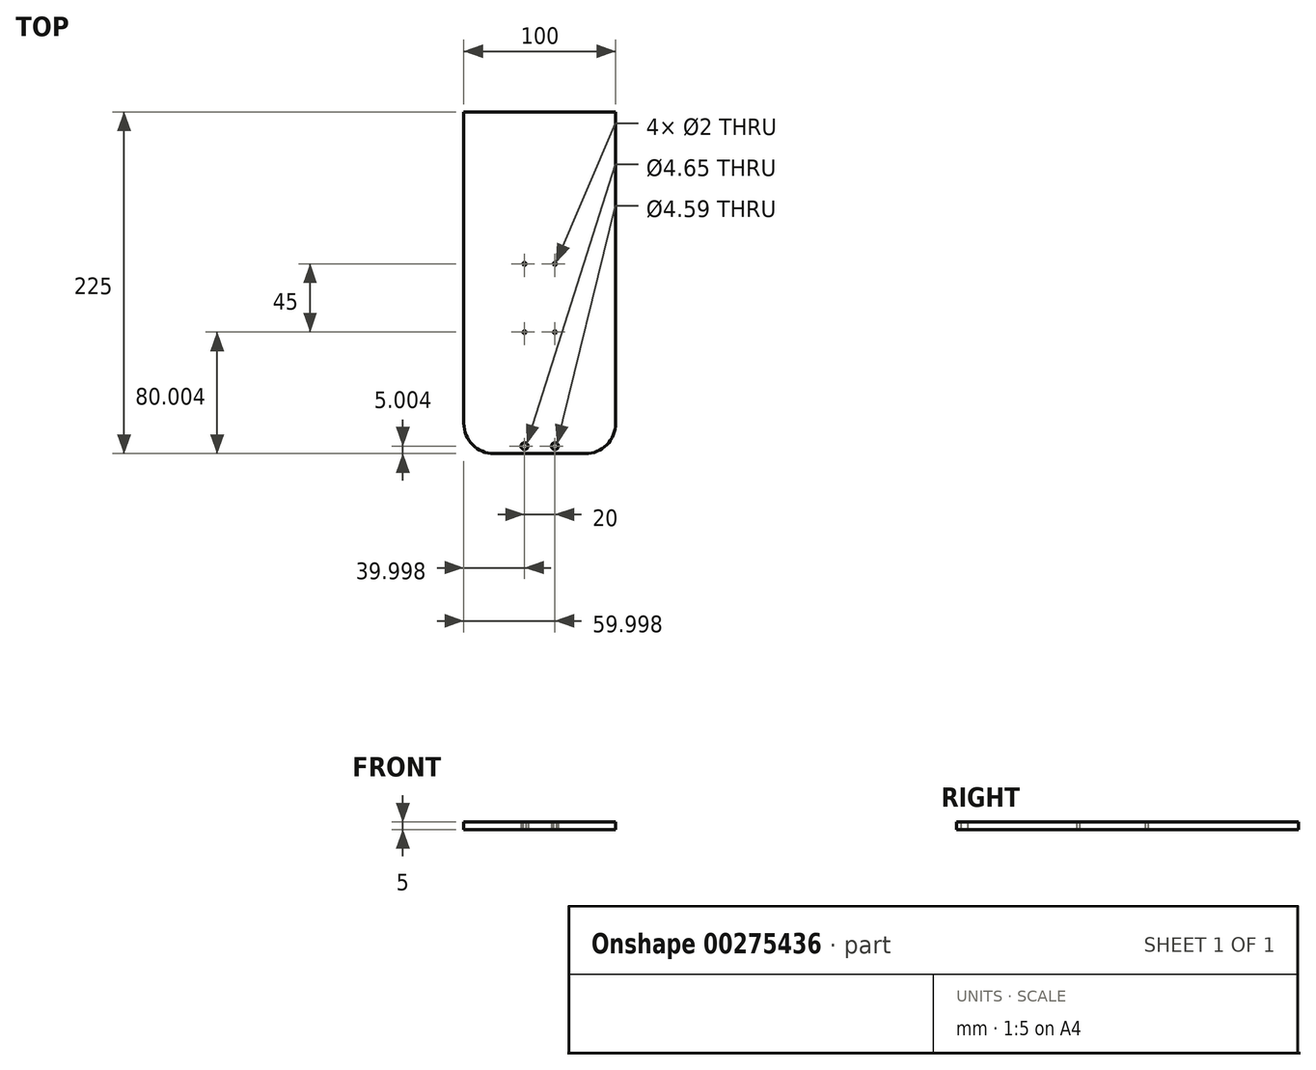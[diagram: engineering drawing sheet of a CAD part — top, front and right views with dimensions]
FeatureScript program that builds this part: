
annotation { "Feature Type Name" : "Feature", "Feature Type Description" : "" }
export const myFeature = defineFeature(function(context is Context, id is Id, definition is map)
    precondition{}
    {
        {
            var Q0;
            Q0=qCreatedBy(makeId("Top.planeOp"),FACE);
            var sketch = newSketch(context, id + "F0", { "sketchPlane" : qUnion([Q0])});
            skLineSegment(sketch, "E0.bottom", {"start": v(-38.9, 102.67) * mm, "end": v(61.1, 102.67) * mm});
            skLineSegment(sketch, "E0.top", {"start": v(-18.9, -122.33) * mm, "end": v(41.1, -122.33) * mm});
            skLineSegment(sketch, "E0.left", {"start": v(-38.9, 102.67) * mm, "end": v(-38.9, -102.33) * mm});
            skLineSegment(sketch, "E0.right", {"start": v(61.1, 102.67) * mm, "end": v(61.1, -102.33) * mm});
            skLineSegment(sketch, "E1", {"start": v(-38.9, -82.33) * mm, "end": v(61.1, -82.33) * mm});
            skLineSegment(sketch, "E2", {"start": v(-28.9, -77.33) * mm, "end": v(-18.9, -77.33) * mm});
            skLineSegment(sketch, "E3", {"start": v(-28.9, -32.33) * mm, "end": v(-18.9, -32.33) * mm});
            skLineSegment(sketch, "E4", {"start": v(-38.9, 12.67) * mm, "end": v(61.1, 12.67) * mm});
            skLineSegment(sketch, "E5", {"start": v(11.1, -122.33) * mm, "end": v(11.1, 114.69) * mm, "construction": true});
            skPoint(sketch, "E5.endSnap0", {"position": v(11.1, 102.67) * mm});
            skLineSegment(sketch, "E6.top", {"start": v(26.1, 7.67) * mm, "end": v(-3.9, 7.67) * mm});
            skLineSegment(sketch, "E6.left", {"start": v(31.1, -32.33) * mm, "end": v(31.1, 2.67) * mm});
            skLineSegment(sketch, "E6.right", {"start": v(-8.9, -32.33) * mm, "end": v(-8.9, 2.67) * mm});
            skLineSegment(sketch, "E7.top", {"start": v(-3.9, -37.33) * mm, "end": v(26.1, -37.33) * mm});
            skLineSegment(sketch, "E7.left", {"start": v(-8.9, -77.33) * mm, "end": v(-8.9, -42.33) * mm});
            skLineSegment(sketch, "E7.right", {"start": v(31.1, -77.33) * mm, "end": v(31.1, -42.33) * mm});
            skPoint(sketch, "E8.visualSharp", {"position": v(-8.9, 7.67) * mm});
            skArc(sketch, "E8.filletArc", {"start": v(-3.9, 7.67) * mm, "mid": v(-7.44, 6.2) * mm, "end": v(-8.9, 2.67) * mm});
            skPoint(sketch, "E9.visualSharp", {"position": v(31.1, 7.67) * mm});
            skArc(sketch, "E9.filletArc", {"start": v(31.1, 2.67) * mm, "mid": v(29.63, 6.2) * mm, "end": v(26.1, 7.67) * mm});
            skPoint(sketch, "E10.visualSharp", {"position": v(-8.9, -37.33) * mm});
            skArc(sketch, "E10.filletArc", {"start": v(-3.9, -37.33) * mm, "mid": v(-7.44, -38.8) * mm, "end": v(-8.9, -42.33) * mm});
            skPoint(sketch, "E11.visualSharp", {"position": v(31.1, -37.33) * mm});
            skArc(sketch, "E11.filletArc", {"start": v(31.1, -42.33) * mm, "mid": v(29.63, -38.8) * mm, "end": v(26.1, -37.33) * mm});
            skCircle(sketch, "E12", {"center": v(1.1, 2.67) * mm, "radius": 1 * mm});
            skCircle(sketch, "E13", {"center": v(21.1, 2.67) * mm, "radius": 1 * mm});
            skCircle(sketch, "E14", {"center": v(1.1, -42.33) * mm, "radius": 1 * mm});
            skCircle(sketch, "E15", {"center": v(21.1, -42.33) * mm, "radius": 1 * mm});
            skPoint(sketch, "E16.visualSharp", {"position": v(-38.9, -122.33) * mm});
            skArc(sketch, "E16.filletArc", {"start": v(-38.9, -102.33) * mm, "mid": v(-33.04, -116.47) * mm, "end": v(-18.9, -122.33) * mm});
            skPoint(sketch, "E17.visualSharp", {"position": v(61.1, -122.33) * mm});
            skArc(sketch, "E17.filletArc", {"start": v(41.1, -122.33) * mm, "mid": v(55.24, -116.47) * mm, "end": v(61.1, -102.33) * mm});
            skCircle(sketch, "E18", {"center": v(1.1, -117.33) * mm, "radius": 2.33 * mm});
            skCircle(sketch, "E19", {"center": v(21.1, -117.33) * mm, "radius": 2.3 * mm});
            skLineSegment(sketch, "E20.bottom", {"start": v(-26.9, -32.33) * mm, "end": v(-20.9, -32.33) * mm});
            skLineSegment(sketch, "E20.left", {"start": v(-28.9, -30.33) * mm, "end": v(-28.9, 7.67) * mm});
            skLineSegment(sketch, "E20.right", {"start": v(-18.9, -30.33) * mm, "end": v(-18.9, 7.67) * mm});
            skLineSegment(sketch, "E21.trimOffspring", {"start": v(43.1, -32.33) * mm, "end": v(49.1, -32.33) * mm});
            skPoint(sketch, "E22.visualSharp", {"position": v(-28.9, -32.33) * mm});
            skArc(sketch, "E22.filletArc", {"start": v(-28.9, -30.33) * mm, "mid": v(-28.32, -31.74) * mm, "end": v(-26.9, -32.33) * mm});
            skPoint(sketch, "E23.visualSharp", {"position": v(-18.9, -32.33) * mm});
            skArc(sketch, "E23.filletArc", {"start": v(-20.9, -32.33) * mm, "mid": v(-19.49, -31.74) * mm, "end": v(-18.9, -30.33) * mm});
            skLineSegment(sketch, "E24.MirrorCS", {"start": v(51.1, -30.33) * mm, "end": v(51.1, 7.67) * mm});
            skLineSegment(sketch, "E25.MirrorCS", {"start": v(41.1, -30.33) * mm, "end": v(41.1, 7.67) * mm});
            skLineSegment(sketch, "E26.MirrorCS", {"start": v(49.1, -32.33) * mm, "end": v(43.1, -32.33) * mm});
            skArc(sketch, "E27.MirrorCS", {"start": v(43.1, -32.33) * mm, "mid": v(41.68, -31.74) * mm, "end": v(41.1, -30.33) * mm});
            skArc(sketch, "E28.MirrorCS", {"start": v(51.1, -30.33) * mm, "mid": v(50.51, -31.74) * mm, "end": v(49.1, -32.33) * mm});
            skLineSegment(sketch, "E29.top", {"start": v(-26.9, -77.33) * mm, "end": v(-20.9, -77.33) * mm});
            skLineSegment(sketch, "E29.left", {"start": v(-28.9, -37.33) * mm, "end": v(-28.9, -75.33) * mm});
            skLineSegment(sketch, "E29.right", {"start": v(-18.9, -37.33) * mm, "end": v(-18.9, -75.33) * mm});
            skPoint(sketch, "E30.visualSharp", {"position": v(-28.9, -77.33) * mm});
            skArc(sketch, "E30.filletArc", {"start": v(-28.9, -75.33) * mm, "mid": v(-28.32, -76.74) * mm, "end": v(-26.9, -77.33) * mm});
            skPoint(sketch, "E31.visualSharp", {"position": v(-18.9, -77.33) * mm});
            skArc(sketch, "E31.filletArc", {"start": v(-20.9, -77.33) * mm, "mid": v(-19.49, -76.74) * mm, "end": v(-18.9, -75.33) * mm});
            skLineSegment(sketch, "E32.MirrorCS", {"start": v(51.1, -37.33) * mm, "end": v(51.1, -75.33) * mm});
            skLineSegment(sketch, "E33.MirrorCS", {"start": v(41.1, -37.33) * mm, "end": v(41.1, -75.33) * mm});
            skLineSegment(sketch, "E34.MirrorCS", {"start": v(49.1, -77.33) * mm, "end": v(43.1, -77.33) * mm});
            skArc(sketch, "E35.MirrorCS", {"start": v(51.1, -75.33) * mm, "mid": v(50.51, -76.74) * mm, "end": v(49.1, -77.33) * mm});
            skArc(sketch, "E36.MirrorCS", {"start": v(43.1, -77.33) * mm, "mid": v(41.68, -76.74) * mm, "end": v(41.1, -75.33) * mm});
            skSolve(sketch);
        }
        {
            var Q0;
            Q0 = qSketchRegion(id + "F0", true);
            extrude(context, id + "F1", {"entities" : qUnion([Q0]), "depth" : 5 * mm, "offsetDistance" : 25 * mm});
        }
    });
